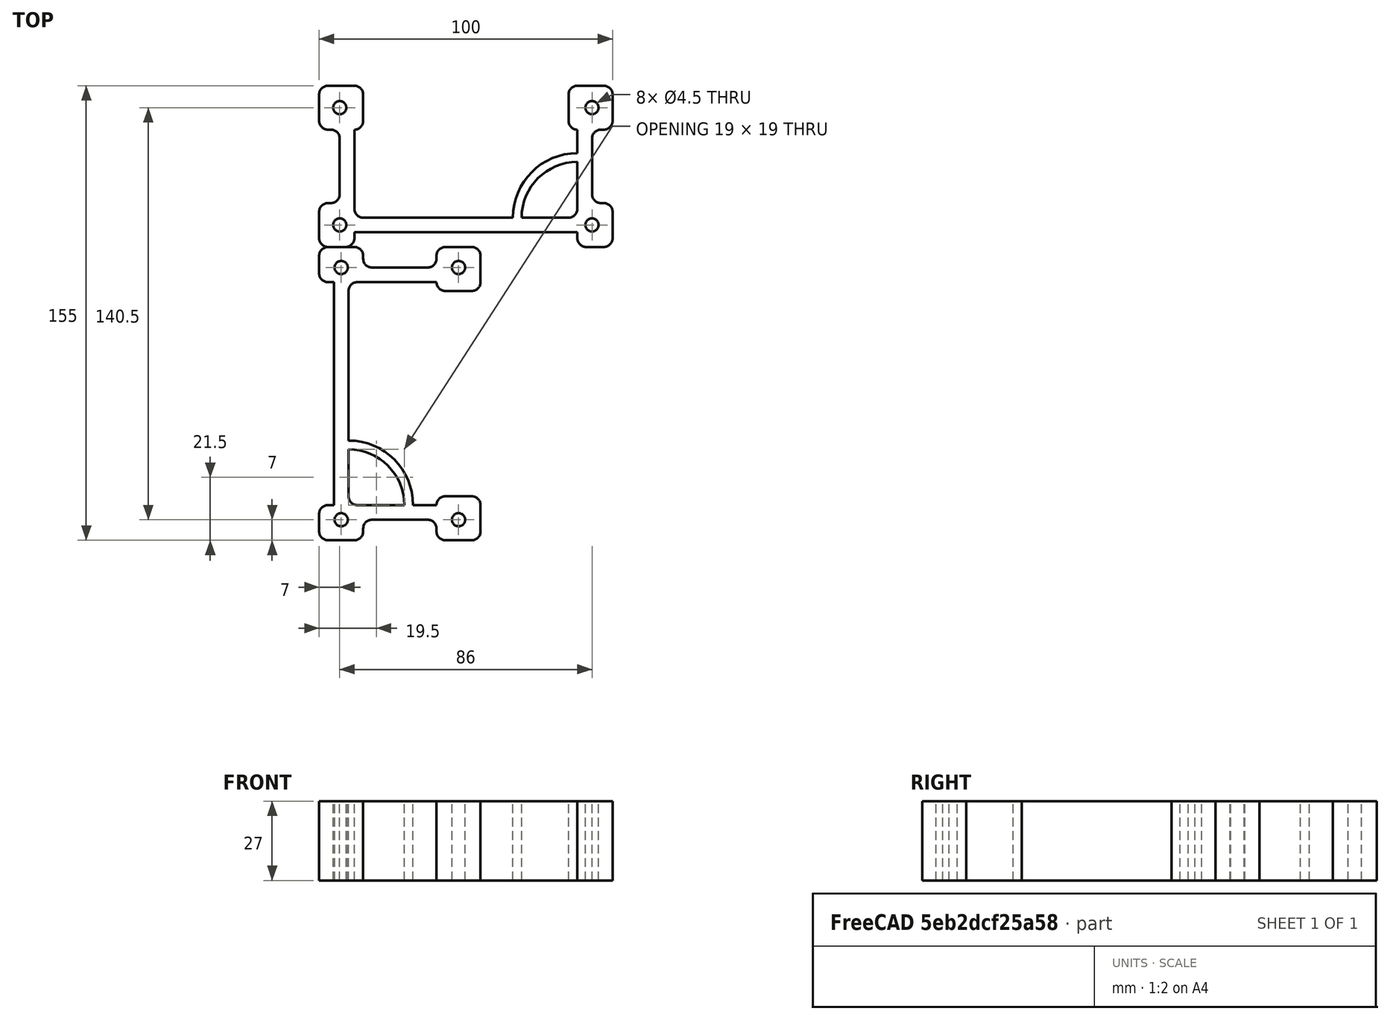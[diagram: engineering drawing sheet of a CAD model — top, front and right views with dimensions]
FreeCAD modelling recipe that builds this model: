
FCSTD DOCUMENT  (FreeCAD 0.15R4630 (Git))
Label: x_tower_right
License: All rights reserved
LicenseURL: http://en.wikipedia.org/wiki/All_rights_reserved
objects: Part::Box×7, Part::Cylinder×6, Part::MultiFuse×5, Part::Fillet×3, Part::Feature×2, Part::Cut×2, Mesh::Feature×1
note: 25 computed .brp shape members not serialized (recipe doc carries the construction recipe); baked Part::Feature solids carry a one-line shape summary decoded from their .brp

FEATURE [Mesh::Feature] towerRight
FEATURE [Part::Feature] towerRight001001  label="towerRight002"
  shape: bbox 100 x 55 x 27 mm, 2111 faces, 0 solids (baked)
FEATURE [Part::Box] Box  label="Cubo"
  Height = 27
  Length = 12
  Width = 15
FEATURE [Part::Box] Box001  label="Cubo001"
  Height = 27
  Length = 12
  Placement = pos=(88,0,0) rot=(0,0,1;0rad)
  Width = 15
FEATURE [Part::Box] Box002  label="Cubo002"
  Height = 27
  Length = 15
  Placement = pos=(85,40,0) rot=(0,0,1;0rad)
  Width = 15
FEATURE [Part::Box] Box003  label="Cubo003"
  Height = 27
  Length = 15
  Placement = pos=(0,40,0) rot=(0,0,1;0rad)
  Width = 15
FEATURE [Part::MultiFuse] Fusion
  Shapes = -> [Box,Box002,Box001,Box003]
FEATURE [Part::Box] Box004  label="Cubo004"
  Height = 27
  Length = 76
  Placement = pos=(12,5,0) rot=(0,0,1;0rad)
  Width = 5
FEATURE [Part::Box] Box005  label="Cubo005"
  Height = 27
  Length = 5
  Placement = pos=(7,15,0) rot=(0,0,1;0rad)
  Width = 25
FEATURE [Part::Box] Box006  label="Cubo006"
  Height = 27
  Length = 5
  Placement = pos=(88,15,0) rot=(0,0,1;0rad)
  Width = 25
FEATURE [Part::MultiFuse] Fusion001
  Shapes = -> [Box005,Box004,Box006]
FEATURE [Part::Cylinder] Cylinder  label="Cilindro"
  Angle = 90
  Height = 27
  Placement = pos=(12,10,0) rot=(0,0,1;0rad)
  Radius = 22
FEATURE [Part::Cylinder] Cylinder001  label="Cilindro001"
  Angle = 90
  Height = 27
  Placement = pos=(12,10,0) rot=(0,0,1;0rad)
  Radius = 19
FEATURE [Part::Cut] Cut
  Base = -> Cylinder
  Placement = pos=(98,-2,0) rot=(0,0,1;1.5708rad)
  Tool = -> Cylinder001
FEATURE [Part::Fillet] Fillet
  Base = -> Fusion
  Edges = 14 edges r=3: [Edge1,Edge3,Edge6,Edge11,Edge13,Edge18,Edge23,Edge25,Edge27,Edge30,Edge37,Edge39,Edge42,Edge47]
FEATURE [Part::MultiFuse] Fusion002
  Shapes = -> [Fusion001,Fillet]
FEATURE [Part::Cylinder] Cylinder002  label="Cilindro002"
  Angle = 360
  Height = 29
  Placement = pos=(7,7.5,-1) rot=(0,0,1;0rad)
  Radius = 2.25
FEATURE [Part::Cylinder] Cylinder003  label="Cilindro003"
  Angle = 360
  Height = 29
  Placement = pos=(7,47.5,-1) rot=(0,0,1;0rad)
  Radius = 2.25
FEATURE [Part::Cylinder] Cylinder004  label="Cilindro004"
  Angle = 360
  Height = 29
  Placement = pos=(93,47.5,-1) rot=(0,0,1;0rad)
  Radius = 2.25
FEATURE [Part::Cylinder] Cylinder005  label="Cilindro005"
  Angle = 360
  Height = 29
  Placement = pos=(93,7.5,-1) rot=(0,0,1;0rad)
  Radius = 2.25
FEATURE [Part::MultiFuse] Fusion005
  Shapes = -> [Cylinder002,Cylinder005,Cylinder004,Cylinder003]
FEATURE [Part::Fillet] Fillet001
  Base = -> Fusion002
  Edges = 2 edges r=3: [Edge61,Edge69]
FEATURE [Part::Fillet] Fillet002
  Base = -> Fillet001
  Edges = 4 edges r=3: [Edge25,Edge62,Edge83,Edge120]
FEATURE [Part::MultiFuse] Fusion007
  Shapes = -> [Cut,Fillet002]
FEATURE [Part::Cut] Cut001  label="x_tower_right"
  Base = -> Fusion007
  Tool = -> Fusion005
FEATURE [Part::Feature] Cut002  label="x_tower_right001"
  Placement = pos=(0,0,0) rot=(0,0,-1;1.5708rad)
  shape: bbox 55 x 100 x 27 mm, 52 faces (baked)
